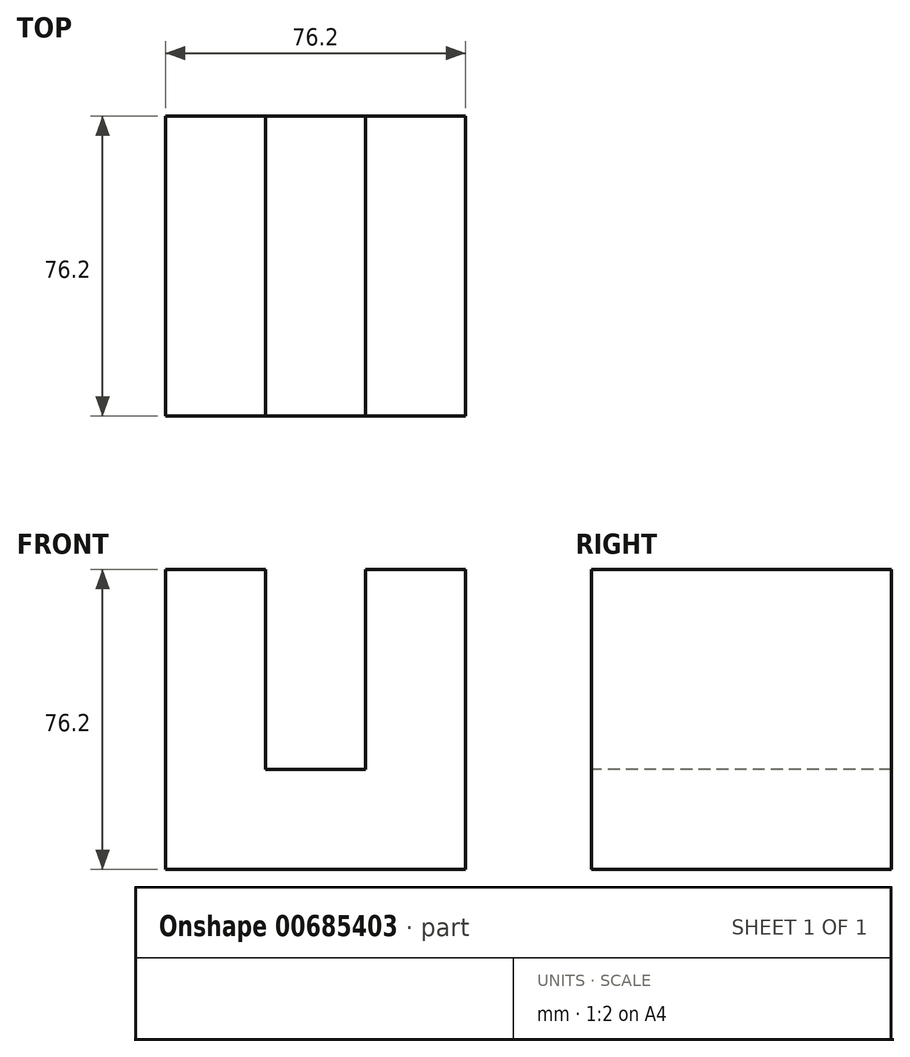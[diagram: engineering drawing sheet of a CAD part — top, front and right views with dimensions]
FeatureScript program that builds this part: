
annotation { "Feature Type Name" : "Feature", "Feature Type Description" : "" }
export const myFeature = defineFeature(function(context is Context, id is Id, definition is map)
    precondition{}
    {
        {
            var Q0;
            Q0=qCreatedBy(makeId("Front.planeOp"),FACE);
            var sketch = newSketch(context, id + "F0", { "sketchPlane" : qUnion([Q0])});
            skLineSegment(sketch, "E0", {"start": v(0, 0) * mm, "end": v(-76.2, 0) * mm});
            skLineSegment(sketch, "E1", {"start": v(-76.2, 0) * mm, "end": v(-76.2, 76.2) * mm});
            skLineSegment(sketch, "E2", {"start": v(-76.2, 76.2) * mm, "end": v(0, 76.2) * mm});
            skLineSegment(sketch, "E3", {"start": v(0, 76.2) * mm, "end": v(0, 0) * mm});
            skSolve(sketch);
        }
        {
            var Q0;
            Q0=makeQuery(id+"F0.imprint","IMPRINT",FACE,{"disambiguationData":[TD([[makeQuery(id+"F0.imprint","IMPRINT",EDGE,{"derivedFrom":sQuery(id+"F0.wireOp",EDGE,"E0")}),-1.0]])]});
            extrude(context, id + "F1", {"entities" : qUnion([Q0]), "depth" : 76.2 * mm, "offsetDistance" : 25.4 * mm});
        }
        {
            var Q0;
            Q0=makeQuery(id+"F1.opExtrude","CAP_FACE",FACE,{"disambiguationData":[OSD([sQuery(id+"F0.wireOp",EDGE,"E0"),sQuery(id+"F0.wireOp",EDGE,"E1"),sQuery(id+"F0.wireOp",EDGE,"E2"),sQuery(id+"F0.wireOp",EDGE,"E3")])],"isStart":false});
            var sketch = newSketch(context, id + "F2", { "sketchPlane" : qUnion([Q0])});
            skLineSegment(sketch, "E4", {"start": v(-38.1, 76.2) * mm, "end": v(-50.8, 76.2) * mm});
            skLineSegment(sketch, "E5", {"start": v(-50.8, 76.2) * mm, "end": v(-50.8, 25.4) * mm});
            skLineSegment(sketch, "E6", {"start": v(-50.8, 25.4) * mm, "end": v(-25.4, 25.4) * mm});
            skLineSegment(sketch, "E7", {"start": v(-25.4, 25.4) * mm, "end": v(-25.4, 76.2) * mm});
            skLineSegment(sketch, "E8", {"start": v(-25.4, 76.2) * mm, "end": v(-38.1, 76.2) * mm});
            skSolve(sketch);
        }
        {
            var Q0;
            Q0=makeQuery(id+"F2.imprint","IMPRINT",FACE,{"disambiguationData":[TD([[makeQuery(id+"F2.imprint","IMPRINT",EDGE,{"derivedFrom":sQuery(id+"F2.wireOp",EDGE,"E4")}),-1.0]])]});
            extrude(context, id + "F3", {"entities" : qUnion([Q0]), "operationType" : NewBodyOperationType.REMOVE, "oppositeDirection" : true, "depth" : 76.2 * mm, "offsetDistance" : 25.4 * mm});
        }
    });
